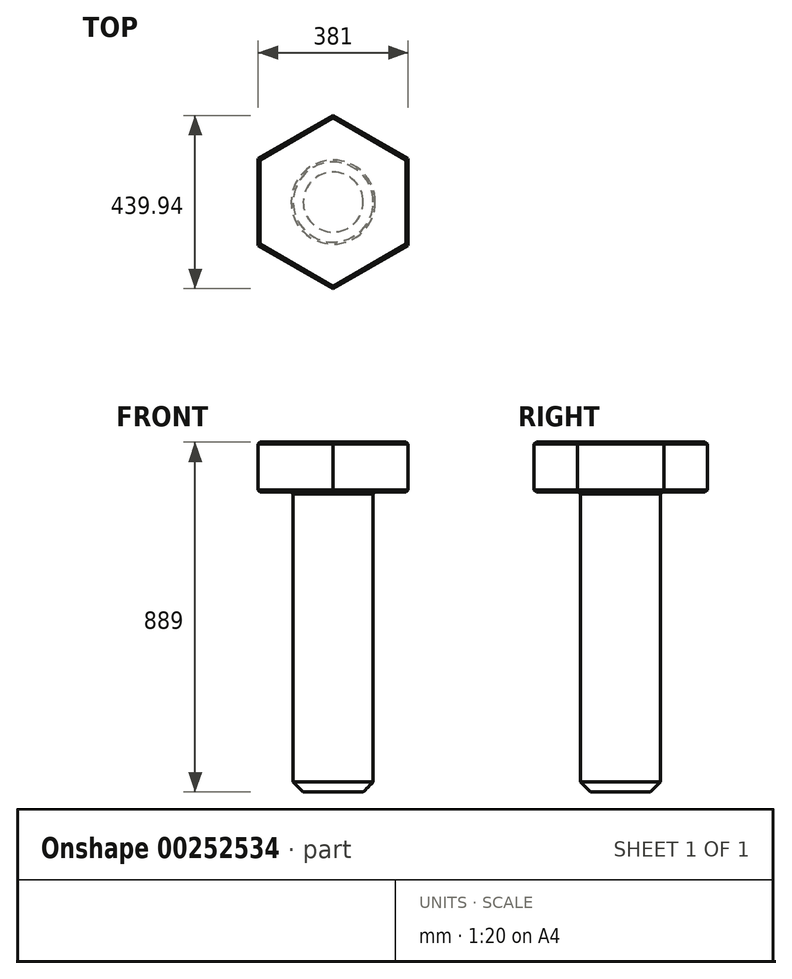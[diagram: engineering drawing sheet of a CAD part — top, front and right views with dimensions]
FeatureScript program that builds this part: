
annotation { "Feature Type Name" : "Feature", "Feature Type Description" : "" }
export const myFeature = defineFeature(function(context is Context, id is Id, definition is map)
    precondition{}
    {
        {
            var Q0;
            Q0=qCreatedBy(makeId("Top.planeOp"),FACE);
            var sketch = newSketch(context, id + "F0", { "sketchPlane" : qUnion([Q0])});
            skCircle(sketch, "E0", {"center": v(0, 0) * mm, "radius": 101.6 * mm});
            skSolve(sketch);
        }
        {
            var Q0;
            Q0=makeQuery(id+"F0.imprint","IMPRINT",FACE,{"disambiguationData":[TD([[makeQuery(id+"F0.imprint","IMPRINT",EDGE,{"derivedFrom":sQuery(id+"F0.wireOp",EDGE,"E0")}),1.0]])]});
            extrude(context, id + "F1", {"entities" : qUnion([Q0]), "depth" : 635 * mm});
        }
        {
            var Q0;
            Q0=makeQuery(id+"F1.opExtrude","CAP_FACE",FACE,{"disambiguationData":[OSD([sQuery(id+"F0.wireOp",EDGE,"E0")])],"isStart":false});
            var sketch = newSketch(context, id + "F2", { "sketchPlane" : qUnion([Q0])});
            skCircle(sketch, "E1.cCircle", {"center": v(0, 0) * mm, "radius": 190.5 * mm, "construction": true});
            skLineSegment(sketch, "E1.0", {"start": v(-190.5, -109.99) * mm, "end": v(-190.5, 109.99) * mm});
            skLineSegment(sketch, "E1.1", {"start": v(-190.5, 109.99) * mm, "end": v(0, 219.97) * mm});
            skLineSegment(sketch, "E1.2", {"start": v(0, 219.97) * mm, "end": v(190.5, 109.99) * mm});
            skLineSegment(sketch, "E1.3", {"start": v(190.5, 109.99) * mm, "end": v(190.5, -109.99) * mm});
            skLineSegment(sketch, "E1.4", {"start": v(190.5, -109.99) * mm, "end": v(0, -219.97) * mm});
            skLineSegment(sketch, "E1.5", {"start": v(0, -219.97) * mm, "end": v(-190.5, -109.99) * mm});
            skPoint(sketch, "E1.0.midPoint", {"position": v(-190.5, 0) * mm});
            skSolve(sketch);
        }
        {
            var Q0;
            Q0=makeQuery(id+"F2.imprint","IMPRINT",FACE,{"disambiguationData":[TD([[makeQuery(id+"F2.imprint","IMPRINT",EDGE,{"derivedFrom":sQuery(id+"F2.wireOp",EDGE,"E1.0")}),-1.0]])]});
            var Q1;
            Q1=makeQuery(id+"F2.imprint","IMPRINT",FACE,{"disambiguationData":[TD([[makeQuery(id+"F2.imprint","IMPRINT",EDGE,{"derivedFrom":makeQuery(id+"F1.opExtrude","CAP_EDGE",EDGE,{"disambiguationData":[OSD([sQuery(id+"F0.wireOp",EDGE,"E0")])],"isStart":false})}),1.0]])]});
            extrude(context, id + "F3", {"entities" : qUnion([Q0, Q1]), "operationType" : NewBodyOperationType.ADD, "depth" : 127 * mm});
        }
        {
            var Q0;
            Q0=makeQuery(id+"F1.opExtrude","CAP_FACE",FACE,{"disambiguationData":[OSD([sQuery(id+"F0.wireOp",EDGE,"E0")])],"isStart":true});
            extrude(context, id + "F4", {"entities" : qUnion([Q0]), "operationType" : NewBodyOperationType.ADD, "depth" : 127 * mm});
        }
        {
            var Q0;
            Q0=makeQuery(id+"F4.opExtrude","CAP_EDGE",EDGE,{"disambiguationData":[OSD([sQuery(id+"F0.wireOp",EDGE,"E0")])],"isStart":false});
            chamfer(context, id + "F5", {"entities" : qUnion([Q0]), "width" : 25.4 * mm, "tangentPropagation" : true});
        }
        {
            var Q0;
            Q0=makeQuery(id+"F3.opExtrude","CAP_FACE",FACE,{"disambiguationData":[OSD([sQuery(id+"F2.wireOp",EDGE,"E1.0"),sQuery(id+"F2.wireOp",EDGE,"E1.1"),sQuery(id+"F2.wireOp",EDGE,"E1.2"),sQuery(id+"F2.wireOp",EDGE,"E1.3"),sQuery(id+"F2.wireOp",EDGE,"E1.4"),sQuery(id+"F2.wireOp",EDGE,"E1.5")])],"isStart":false});
            var Q1;
            Q1=makeQuery(id+"F3.opExtrude","CAP_FACE",FACE,{"disambiguationData":[OSD([sQuery(id+"F2.wireOp",EDGE,"E1.0"),sQuery(id+"F2.wireOp",EDGE,"E1.1"),sQuery(id+"F2.wireOp",EDGE,"E1.2"),sQuery(id+"F2.wireOp",EDGE,"E1.3"),sQuery(id+"F2.wireOp",EDGE,"E1.4"),sQuery(id+"F2.wireOp",EDGE,"E1.5")])],"isStart":true});
            chamfer(context, id + "F6", {"entities" : qUnion([Q0, Q1]), "width" : 5.08 * mm, "tangentPropagation" : true});
        }
    });
